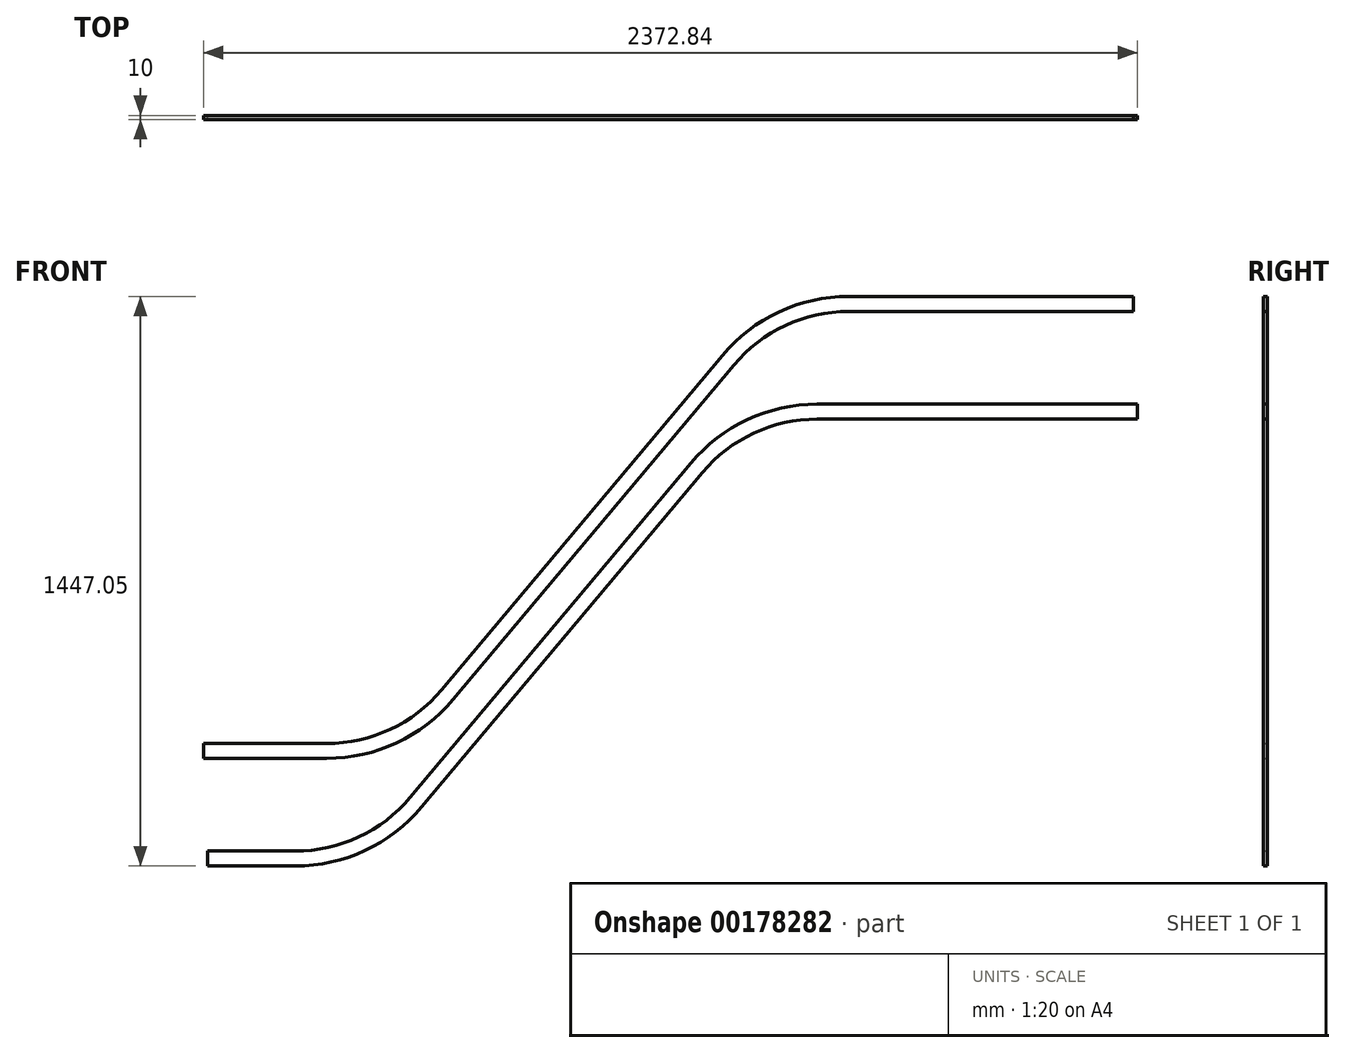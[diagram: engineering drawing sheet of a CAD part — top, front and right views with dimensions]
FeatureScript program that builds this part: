
annotation { "Feature Type Name" : "Feature", "Feature Type Description" : "" }
export const myFeature = defineFeature(function(context is Context, id is Id, definition is map)
    precondition{}
    {
        {
            var Q0;
            Q0=qCreatedBy(makeId("Front.planeOp"),FACE);
            var sketch = newSketch(context, id + "F0", { "sketchPlane" : qUnion([Q0])});
            skArc(sketch, "E0.0", {"start": v(1191.37, 1269.69) * mm, "mid": v(1191.37, 1269.69) * mm, "end": v(1191.36, 1269.69) * mm});
            skLineSegment(sketch, "E1", {"start": v(1191.36, 1269.69) * mm, "end": v(1191.37, 1269.69) * mm});
            skLineSegment(sketch, "E2", {"start": v(-506.45, 209.13) * mm, "end": v(-192.98, 209.13) * mm, "construction": true});
            skLineSegment(sketch, "E3", {"start": v(-495.95, -64.37) * mm, "end": v(-272.98, -64.37) * mm, "construction": true});
            skPoint(sketch, "E4", {"position": v(-506.45, 228.13) * mm});
            skPoint(sketch, "E5", {"position": v(-506.45, 190.13) * mm});
            skPoint(sketch, "E6", {"position": v(-495.95, -45.37) * mm});
            skPoint(sketch, "E7", {"position": v(-495.95, -83.37) * mm});
            skPoint(sketch, "E8", {"position": v(1866.39, 1052.18) * mm});
            skPoint(sketch, "E9", {"position": v(1866.39, 1090.18) * mm});
            skPoint(sketch, "E10", {"position": v(1856.39, 1325.68) * mm});
            skPoint(sketch, "E11", {"position": v(1856.39, 1363.68) * mm});
            skPoint(sketch, "E12.visualSharp", {"position": v(-6.45, 209.13) * mm});
            skPoint(sketch, "E13.visualSharp", {"position": v(-86.45, -64.37) * mm});
            skPoint(sketch, "E14.visualSharp", {"position": v(866.39, 1071.18) * mm});
            skPoint(sketch, "E15.visualSharp", {"position": v(946.39, 1344.68) * mm});
            skLineSegment(sketch, "E16", {"start": v(1866.39, 1052.18) * mm, "end": v(1866.39, 1090.18) * mm});
            skLineSegment(sketch, "E17", {"start": v(1856.39, 1325.68) * mm, "end": v(1856.39, 1363.68) * mm});
            skPoint(sketch, "E18.end.orphan", {"position": v(1866.39, 1071.18) * mm});
            skPoint(sketch, "E19.end.orphan", {"position": v(1856.39, 1344.68) * mm});
            skLineSegment(sketch, "E20", {"start": v(1052.9, 1071.18) * mm, "end": v(1866.39, 1071.18) * mm, "construction": true});
            skLineSegment(sketch, "E21", {"start": v(1132.9, 1344.68) * mm, "end": v(1856.39, 1344.68) * mm, "construction": true});
            skLineSegment(sketch, "E22", {"start": v(113.44, 352.01) * mm, "end": v(826.5, 1201.8) * mm, "construction": true});
            skLineSegment(sketch, "E23", {"start": v(33.44, 78.51) * mm, "end": v(746.5, 928.3) * mm, "construction": true});
            skLineSegment(sketch, "E24", {"start": v(-506.45, 190.13) * mm, "end": v(-506.45, 228.13) * mm});
            skLineSegment(sketch, "E25", {"start": v(-495.95, -83.37) * mm, "end": v(-495.95, -45.37) * mm});
            skArc(sketch, "E26.filletArc", {"start": v(-192.98, 209.13) * mm, "mid": v(-23.93, 246.6) * mm, "end": v(113.44, 352.01) * mm, "construction": true});
            skArc(sketch, "E27.filletArc", {"start": v(-272.98, -64.37) * mm, "mid": v(-103.93, -26.9) * mm, "end": v(33.44, 78.51) * mm, "construction": true});
            skArc(sketch, "E28.filletArc", {"start": v(1052.9, 1071.18) * mm, "mid": v(883.86, 1033.7) * mm, "end": v(746.5, 928.3) * mm, "construction": true});
            skArc(sketch, "E29.filletArc", {"start": v(1132.9, 1344.68) * mm, "mid": v(963.86, 1307.2) * mm, "end": v(826.5, 1201.8) * mm, "construction": true});
            skArc(sketch, "E30.0", {"start": v(-192.98, 228.13) * mm, "mid": v(-31.96, 263.83) * mm, "end": v(98.89, 364.23) * mm});
            skArc(sketch, "E31.0", {"start": v(-192.98, 190.13) * mm, "mid": v(-15.9, 229.39) * mm, "end": v(128, 339.8) * mm});
            skArc(sketch, "E32.0", {"start": v(-272.98, -83.37) * mm, "mid": v(-95.9, -44.11) * mm, "end": v(48, 66.3) * mm});
            skArc(sketch, "E33.0", {"start": v(-272.98, -45.37) * mm, "mid": v(-111.96, -9.67) * mm, "end": v(18.89, 90.73) * mm});
            skArc(sketch, "E34.0", {"start": v(1132.9, 1363.68) * mm, "mid": v(955.83, 1324.43) * mm, "end": v(811.94, 1214.01) * mm});
            skArc(sketch, "E35.0", {"start": v(1052.9, 1090.18) * mm, "mid": v(875.83, 1050.93) * mm, "end": v(731.94, 940.51) * mm});
            skArc(sketch, "E36.0", {"start": v(1132.9, 1325.68) * mm, "mid": v(971.9, 1289.99) * mm, "end": v(841.05, 1189.58) * mm});
            skArc(sketch, "E37.0", {"start": v(1052.9, 1052.18) * mm, "mid": v(891.9, 1016.49) * mm, "end": v(761.05, 916.08) * mm});
            skLineSegment(sketch, "E38", {"start": v(1856.39, 1363.68) * mm, "end": v(1132.9, 1363.68) * mm});
            skLineSegment(sketch, "E39", {"start": v(1132.9, 1325.68) * mm, "end": v(1856.39, 1325.68) * mm});
            skLineSegment(sketch, "E40", {"start": v(1866.39, 1090.18) * mm, "end": v(1052.9, 1090.18) * mm});
            skLineSegment(sketch, "E41", {"start": v(1052.9, 1052.18) * mm, "end": v(1866.39, 1052.18) * mm});
            skLineSegment(sketch, "E42", {"start": v(841.05, 1189.58) * mm, "end": v(128, 339.8) * mm});
            skLineSegment(sketch, "E43", {"start": v(98.89, 364.23) * mm, "end": v(811.94, 1214.01) * mm});
            skLineSegment(sketch, "E44", {"start": v(731.94, 940.51) * mm, "end": v(18.89, 90.73) * mm});
            skLineSegment(sketch, "E45", {"start": v(48, 66.3) * mm, "end": v(761.05, 916.08) * mm});
            skLineSegment(sketch, "E46", {"start": v(-192.98, 228.13) * mm, "end": v(-506.45, 228.13) * mm});
            skLineSegment(sketch, "E47", {"start": v(-506.45, 190.13) * mm, "end": v(-192.98, 190.13) * mm});
            skLineSegment(sketch, "E48", {"start": v(-272.98, -45.37) * mm, "end": v(-495.95, -45.37) * mm});
            skLineSegment(sketch, "E49", {"start": v(-495.95, -83.37) * mm, "end": v(-272.98, -83.37) * mm});
            skSolve(sketch);
        }
        {
            var Q0;
            Q0=qSketchRegion(id+"F0",true);
            extrude(context, id + "F1", {"entities" : qUnion([Q0]), "depth" : 10 * mm});
        }
    });
